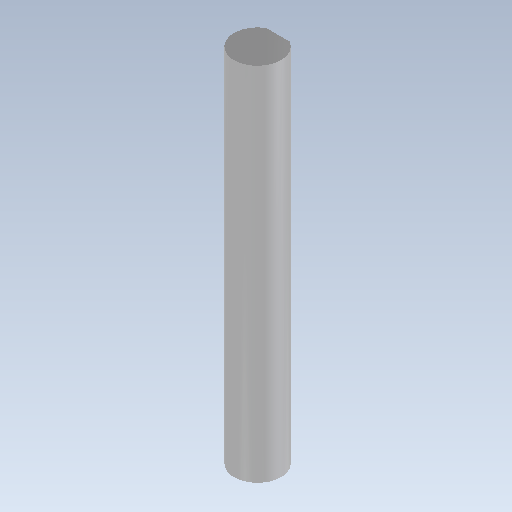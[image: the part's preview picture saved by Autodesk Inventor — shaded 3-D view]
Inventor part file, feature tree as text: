
AUTODESK INVENTOR PART (.ipt)
format: ipt  version: 2020 (Build 240168000, 168)  size: 88,576 bytes
history: native  units: mm
features: extrude x2, sketch x2
ambient origin geometry x8: Origin, YZ Plane, XZ Plane, XY Plane, X Axis, Y Axis, Z Axis, Center Point
bodies: Solid1 (feature_tree)
feature tree (4):
  extrude  "Extrusion1"  Depth=23.0mm TaperAngle=0.0deg
  extrude  "Extrusion2"  Depth=23.0mm TaperAngle=0.0deg
  sketch  "Sketch1"  dims[d0=3.0mm d1=23.0mm d2=0.0mm]
  sketch  "Sketch2"  dims[d3=1.3mm d4=23.0mm d5=0.0mm]
